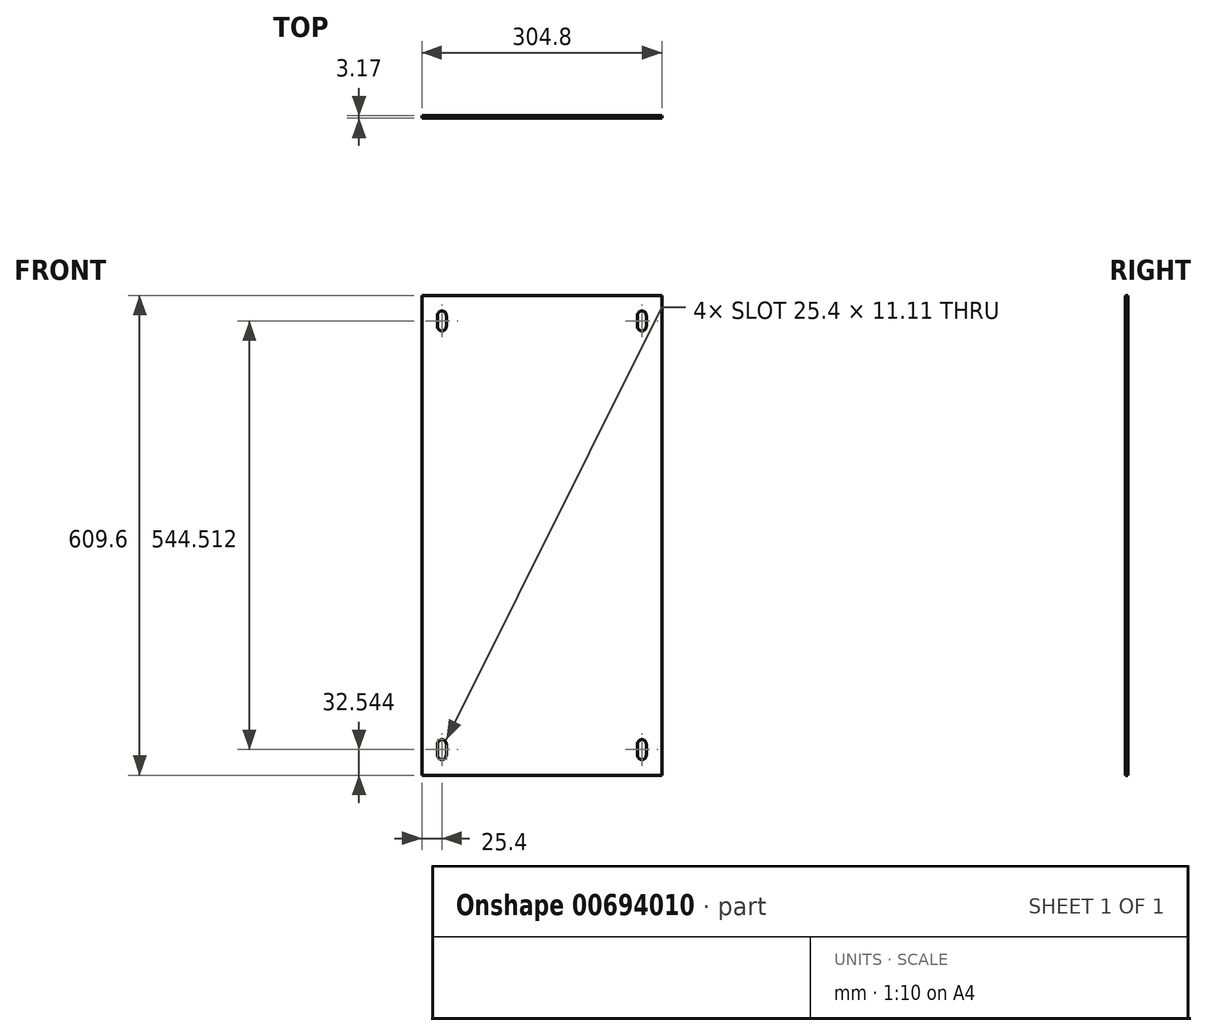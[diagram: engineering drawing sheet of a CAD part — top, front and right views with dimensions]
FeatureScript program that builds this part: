
annotation { "Feature Type Name" : "Feature", "Feature Type Description" : "" }
export const myFeature = defineFeature(function(context is Context, id is Id, definition is map)
    precondition{}
    {
        {
            var Q0;
            Q0=qCreatedBy(makeId("Front.planeOp"),FACE);
            var sketch = newSketch(context, id + "F0", { "sketchPlane" : qUnion([Q0])});
            skLineSegment(sketch, "E0.bottom", {"start": v(-152.4, 304.8) * mm, "end": v(152.4, 304.8) * mm});
            skLineSegment(sketch, "E0.top", {"start": v(-152.4, -304.8) * mm, "end": v(152.4, -304.8) * mm});
            skLineSegment(sketch, "E0.left", {"start": v(-152.4, 304.8) * mm, "end": v(-152.4, -304.8) * mm});
            skLineSegment(sketch, "E0.right", {"start": v(152.4, 304.8) * mm, "end": v(152.4, -304.8) * mm});
            skLineSegment(sketch, "E1", {"start": v(-152.4, 0) * mm, "end": v(152.4, 0) * mm, "construction": true});
            skArc(sketch, "E2", {"start": v(-121.44, 279.4) * mm, "mid": v(-127, 284.96) * mm, "end": v(-132.56, 279.4) * mm});
            skArc(sketch, "E3", {"start": v(-132.56, 265.11) * mm, "mid": v(-127, 259.56) * mm, "end": v(-121.44, 265.11) * mm});
            skLineSegment(sketch, "E4", {"start": v(-132.56, 279.4) * mm, "end": v(-132.56, 265.11) * mm});
            skLineSegment(sketch, "E5", {"start": v(-121.44, 279.4) * mm, "end": v(-121.44, 265.11) * mm});
            skLineSegment(sketch, "E6.MirrorCS", {"start": v(132.56, 279.4) * mm, "end": v(132.56, 265.11) * mm});
            skLineSegment(sketch, "E7.MirrorCS", {"start": v(121.44, 279.4) * mm, "end": v(121.44, 265.11) * mm});
            skArc(sketch, "E8.MirrorCS", {"start": v(132.56, 265.11) * mm, "mid": v(127, 259.56) * mm, "end": v(121.44, 265.11) * mm});
            skArc(sketch, "E9.MirrorCS", {"start": v(121.44, 279.4) * mm, "mid": v(127, 284.96) * mm, "end": v(132.56, 279.4) * mm});
            skArc(sketch, "E10.MirrorCS", {"start": v(121.44, -279.4) * mm, "mid": v(127, -284.96) * mm, "end": v(132.56, -279.4) * mm});
            skArc(sketch, "E11.MirrorCS", {"start": v(132.56, -265.11) * mm, "mid": v(127, -259.56) * mm, "end": v(121.44, -265.11) * mm});
            skLineSegment(sketch, "E12.MirrorCS", {"start": v(121.44, -279.4) * mm, "end": v(121.44, -265.11) * mm});
            skLineSegment(sketch, "E13.MirrorCS", {"start": v(132.56, -279.4) * mm, "end": v(132.56, -265.11) * mm});
            skLineSegment(sketch, "E14.MirrorCS", {"start": v(-132.56, -279.4) * mm, "end": v(-132.56, -265.11) * mm});
            skLineSegment(sketch, "E15.MirrorCS", {"start": v(-121.44, -279.4) * mm, "end": v(-121.44, -265.11) * mm});
            skArc(sketch, "E16.MirrorCS", {"start": v(-121.44, -279.4) * mm, "mid": v(-127, -284.96) * mm, "end": v(-132.56, -279.4) * mm});
            skArc(sketch, "E17.MirrorCS", {"start": v(-132.56, -265.11) * mm, "mid": v(-127, -259.56) * mm, "end": v(-121.44, -265.11) * mm});
            skSolve(sketch);
        }
        {
            var Q0;
            Q0=makeQuery(id+"F0.imprint","IMPRINT",FACE,{"disambiguationData":[TD([[makeQuery(id+"F0.imprint","IMPRINT",EDGE,{"derivedFrom":sQuery(id+"F0.wireOp",EDGE,"E0.bottom")}),-1.0]])]});
            extrude(context, id + "F1", {"entities" : qUnion([Q0]), "depth" : 3.17 * mm, "offsetDistance" : 25.4 * mm});
        }
    });
